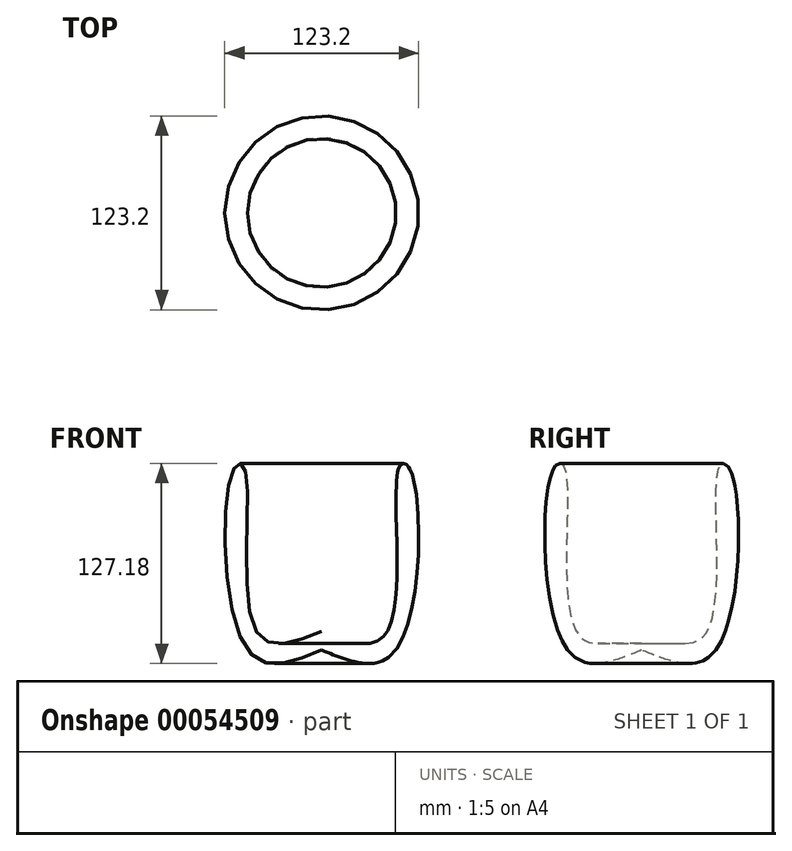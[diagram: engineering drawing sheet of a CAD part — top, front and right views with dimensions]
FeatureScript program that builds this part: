
annotation { "Feature Type Name" : "Feature", "Feature Type Description" : "" }
export const myFeature = defineFeature(function(context is Context, id is Id, definition is map)
    precondition{}
    {
        {
            var Q0;
            Q0=qCreatedBy(makeId("Front.planeOp"),FACE);
            var sketch = newSketch(context, id + "F0", { "sketchPlane" : qUnion([Q0])});
            skFitSpline(sketch, "E0", {"points": [v(0, -69.72) * mm, v(-41.57, -69.72) * mm, v(-49.37, 35.08) * mm, v(-55.87, 33.78) * mm, v(-46.77, -81.85) * mm, v(0, -81.42) * mm], "startDerivative": vector(-290.39, -113.45) * mm, "endDerivative": vector(288.7, 119.59) * mm});
            skLineSegment(sketch, "E1", {"start": v(0, -98.3) * mm, "end": v(0, 74.05) * mm});
            skSolve(sketch);
        }
        {
            var Q0;
            {var subQ0=sQuery(id+"F0.wireOp",EDGE,"E0");Q0=makeQuery(id+"F0.imprint","IMPRINT",FACE,{"disambiguationData":[TD([[makeQuery(id+"F0.imprint","IMPRINT",EDGE,{"derivedFrom":subQ0}),1.0]])]});}
            var Q1;
            Q1=sQuery(id+"F0.wireOp",EDGE,"E1");
            revolve(context, id + "F1", {"entities" : qUnion([Q0]), "axis" : qUnion([Q1]), "revolveType" : RevolveType.FULL});
        }
    });
